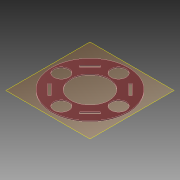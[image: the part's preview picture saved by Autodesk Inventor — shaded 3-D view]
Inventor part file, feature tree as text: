
AUTODESK INVENTOR PART (.ipt)
format: ipt  version: 2021.3 (Build 253353000, 353)  size: 156,672 bytes
history: native  units: mm
features: other x5, extrude x1, sketch x1, reference x1
ambient origin geometry x8: Origin, YZ Plane, XZ Plane, XY Plane, X Axis, Y Axis, Z Axis, Center Point
bodies: Body1 (feature_tree)
feature tree (8):
  other  "Твердое тело1"
  other  "РабПлоскость1"
  extrude  "Выдавливание1"  Depth=202.0mm
  sketch  "Эскиз1"
  reference  "Ссылка1"
  parser-record x1  (decoder bookkeeping rows leaked as tree rows — omitted from the tree; the rows remain in map.json)
  other  "Поворотный_модуль_В5.iam"
  other  "Диск_опорный_В5:1"
note: 1 file-system path scrubbed to <path> (originals preserved in map.json)
